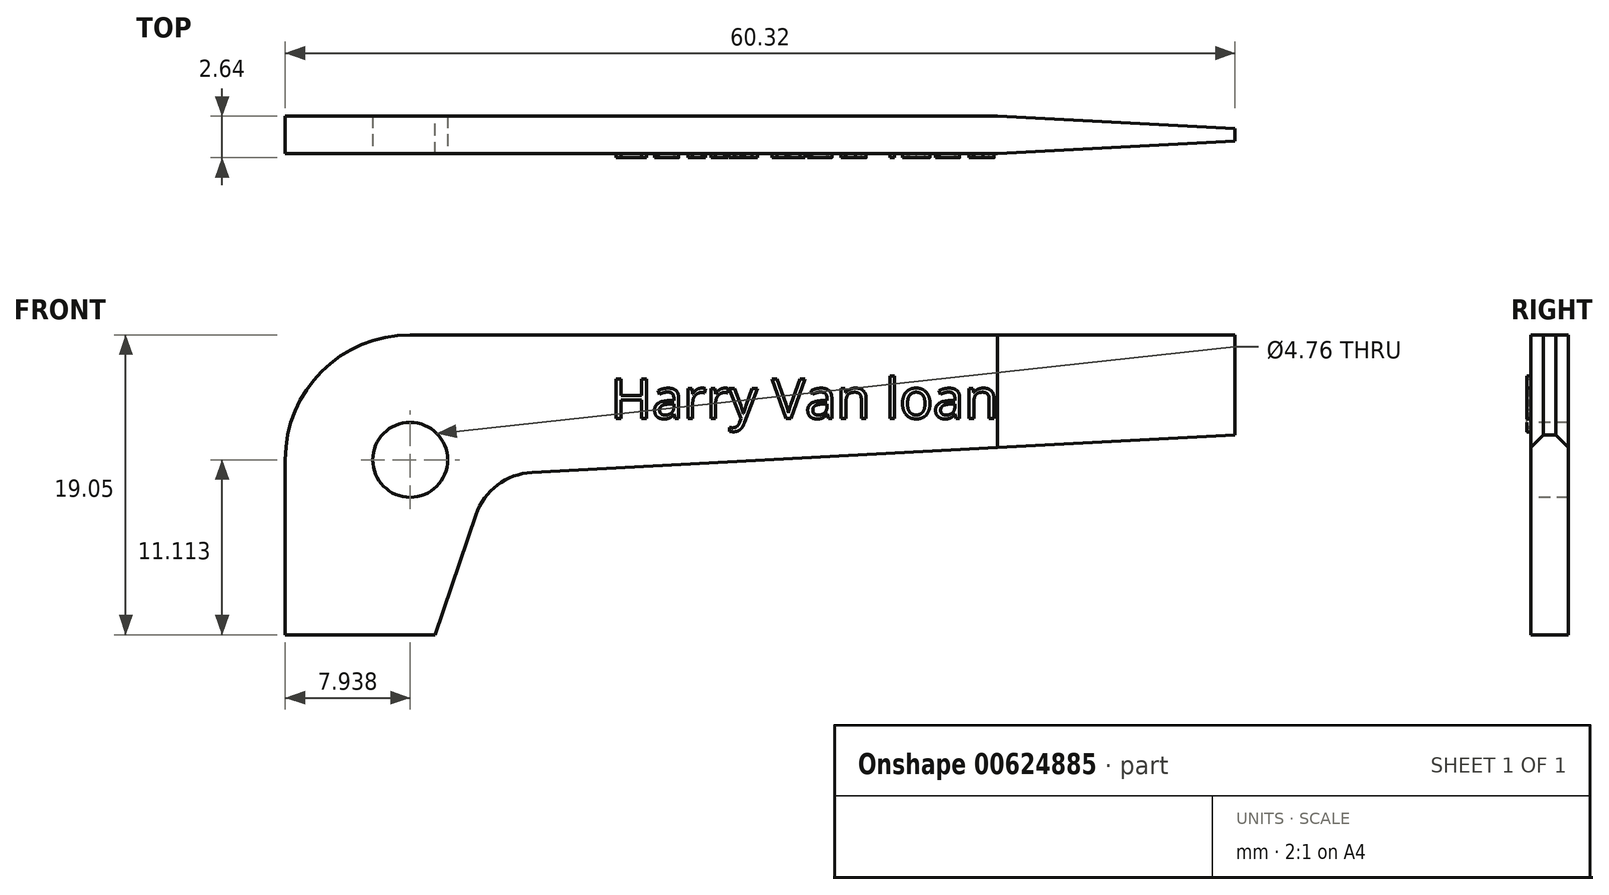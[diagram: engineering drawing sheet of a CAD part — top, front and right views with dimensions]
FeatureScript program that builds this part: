
annotation { "Feature Type Name" : "Feature", "Feature Type Description" : "" }
export const myFeature = defineFeature(function(context is Context, id is Id, definition is map)
    precondition{}
    {
        {
            var Q0;
            Q0=qCreatedBy(makeId("Front.planeOp"),FACE);
            var sketch = newSketch(context, id + "F0", { "sketchPlane" : qUnion([Q0])});
            skLineSegment(sketch, "E0.top", {"start": v(7.94, 19.05) * mm, "end": v(60.33, 19.05) * mm});
            skLineSegment(sketch, "E0.left", {"start": v(0, 0) * mm, "end": v(0, 11.11) * mm});
            skLineSegment(sketch, "E1", {"start": v(9.53, 0) * mm, "end": v(12.12, 7.63) * mm});
            skLineSegment(sketch, "E2", {"start": v(60.33, 12.7) * mm, "end": v(15.66, 10.31) * mm});
            skLineSegment(sketch, "E3", {"start": v(9.53, 0) * mm, "end": v(0, 0) * mm});
            skLineSegment(sketch, "E4", {"start": v(60.33, 12.7) * mm, "end": v(60.33, 19.05) * mm});
            skArc(sketch, "E5", {"start": v(15.66, 10.31) * mm, "mid": v(13.48, 9.51) * mm, "end": v(12.12, 7.63) * mm});
            skPoint(sketch, "E6.visualSharp", {"position": v(0, 19.05) * mm});
            skArc(sketch, "E6.filletArc", {"start": v(7.94, 19.05) * mm, "mid": v(2.32, 16.73) * mm, "end": v(0, 11.11) * mm});
            skSolve(sketch);
        }
        {
            var Q0;
            Q0=makeQuery(id+"F0.imprint","IMPRINT",FACE,{"disambiguationData":[TD([[makeQuery(id+"F0.imprint","IMPRINT",EDGE,{"derivedFrom":sQuery(id+"F0.wireOp",EDGE,"E0.top")}),-1.0]])]});
            extrude(context, id + "F1", {"entities" : qUnion([Q0]), "depth" : 2.38 * mm, "offsetDistance" : 25.4 * mm});
        }
        {
            var Q0;
            Q0=makeQuery(id+"F1.opExtrude","CAP_FACE",FACE,{"disambiguationData":[OSD([sQuery(id+"F0.wireOp",EDGE,"E0.top"),sQuery(id+"F0.wireOp",EDGE,"E0.left"),sQuery(id+"F0.wireOp",EDGE,"E1"),sQuery(id+"F0.wireOp",EDGE,"E2"),sQuery(id+"F0.wireOp",EDGE,"E3"),sQuery(id+"F0.wireOp",EDGE,"E4"),sQuery(id+"F0.wireOp",EDGE,"E5"),sQuery(id+"F0.wireOp",EDGE,"E6.filletArc")])],"isStart":false});
            var sketch = newSketch(context, id + "F2", { "sketchPlane" : qUnion([Q0])});
            skCircle(sketch, "E7", {"center": v(7.94, 11.11) * mm, "radius": 2.38 * mm});
            skSolve(sketch);
        }
        {
            var Q0;
            Q0=makeQuery(id+"F2.imprint","IMPRINT",FACE,{"disambiguationData":[TD([[makeQuery(id+"F2.imprint","IMPRINT",EDGE,{"derivedFrom":sQuery(id+"F2.wireOp",EDGE,"E7")}),1.0]])]});
            extrude(context, id + "F3", {"entities" : qUnion([Q0]), "operationType" : NewBodyOperationType.REMOVE, "oppositeDirection" : true, "depth" : 25.4 * mm, "offsetDistance" : 25.4 * mm});
        }
        {
            var Q0;
            Q0=makeQuery(id+"F1.opExtrude","SWEPT_FACE",FACE,{"disambiguationData":[OSD([sQuery(id+"F0.wireOp",EDGE,"E0.top")])]});
            var sketch = newSketch(context, id + "F4", { "sketchPlane" : qUnion([Q0])});
            skLineSegment(sketch, "E8", {"start": v(45.24, 0) * mm, "end": v(60.33, -0.8) * mm});
            skLineSegment(sketch, "E9", {"start": v(60.33, -0.8) * mm, "end": v(60.33, 0) * mm});
            skLineSegment(sketch, "E10", {"start": v(60.33, 0) * mm, "end": v(45.24, 0) * mm});
            skPoint(sketch, "E11.endSnap0", {"position": v(60.33, -1.2) * mm});
            skLineSegment(sketch, "E12.MirrorCS", {"start": v(45.24, -2.38) * mm, "end": v(60.33, -1.59) * mm});
            skLineSegment(sketch, "E13.MirrorCS", {"start": v(60.33, -2.38) * mm, "end": v(45.24, -2.38) * mm});
            skLineSegment(sketch, "E14.MirrorCS", {"start": v(60.33, -1.59) * mm, "end": v(60.33, -2.38) * mm});
            skSolve(sketch);
        }
        {
            var Q0;
            Q0=makeQuery(id+"F4.imprint","IMPRINT",FACE,{"disambiguationData":[TD([[makeQuery(id+"F4.imprint","IMPRINT",EDGE,{"derivedFrom":sQuery(id+"F4.wireOp",EDGE,"E12.MirrorCS")}),-1.0]])]});
            var Q1;
            Q1=makeQuery(id+"F4.imprint","IMPRINT",FACE,{"disambiguationData":[TD([[makeQuery(id+"F4.imprint","IMPRINT",EDGE,{"derivedFrom":sQuery(id+"F4.wireOp",EDGE,"E8")}),1.0]])]});
            extrude(context, id + "F5", {"entities" : qUnion([Q0, Q1]), "operationType" : NewBodyOperationType.REMOVE, "oppositeDirection" : true, "depth" : 25.4 * mm, "offsetDistance" : 25.4 * mm});
        }
        {
            var Q0;
            Q0=makeQuery(id+"F1.opExtrude","CAP_FACE",FACE,{"disambiguationData":[OSD([sQuery(id+"F0.wireOp",EDGE,"E0.top"),sQuery(id+"F0.wireOp",EDGE,"E0.left"),sQuery(id+"F0.wireOp",EDGE,"E1"),sQuery(id+"F0.wireOp",EDGE,"E2"),sQuery(id+"F0.wireOp",EDGE,"E3"),sQuery(id+"F0.wireOp",EDGE,"E4"),sQuery(id+"F0.wireOp",EDGE,"E5"),sQuery(id+"F0.wireOp",EDGE,"E6.filletArc")])],"isStart":false});
            var sketch = newSketch(context, id + "F6", { "sketchPlane" : qUnion([Q0])});
            skText(sketch, "E15", { "text": "Harry Van loan", "fontName": "NotoSans-Regular.ttf"});
            const initialGuessF6  = {"E15": [0.02068, 0.01374, 1, 0, 0.00254]};
            skSetInitialGuess(sketch, initialGuessF6);
            skSolve(sketch);
        }
        {
            var Q0;
            Q0 = qSketchRegion(id + "F6", true);
            extrude(context, id + "F7", {"entities" : qUnion([Q0]), "operationType" : NewBodyOperationType.ADD, "depth" : 0.25 * mm, "offsetDistance" : 25.4 * mm});
        }
    });
